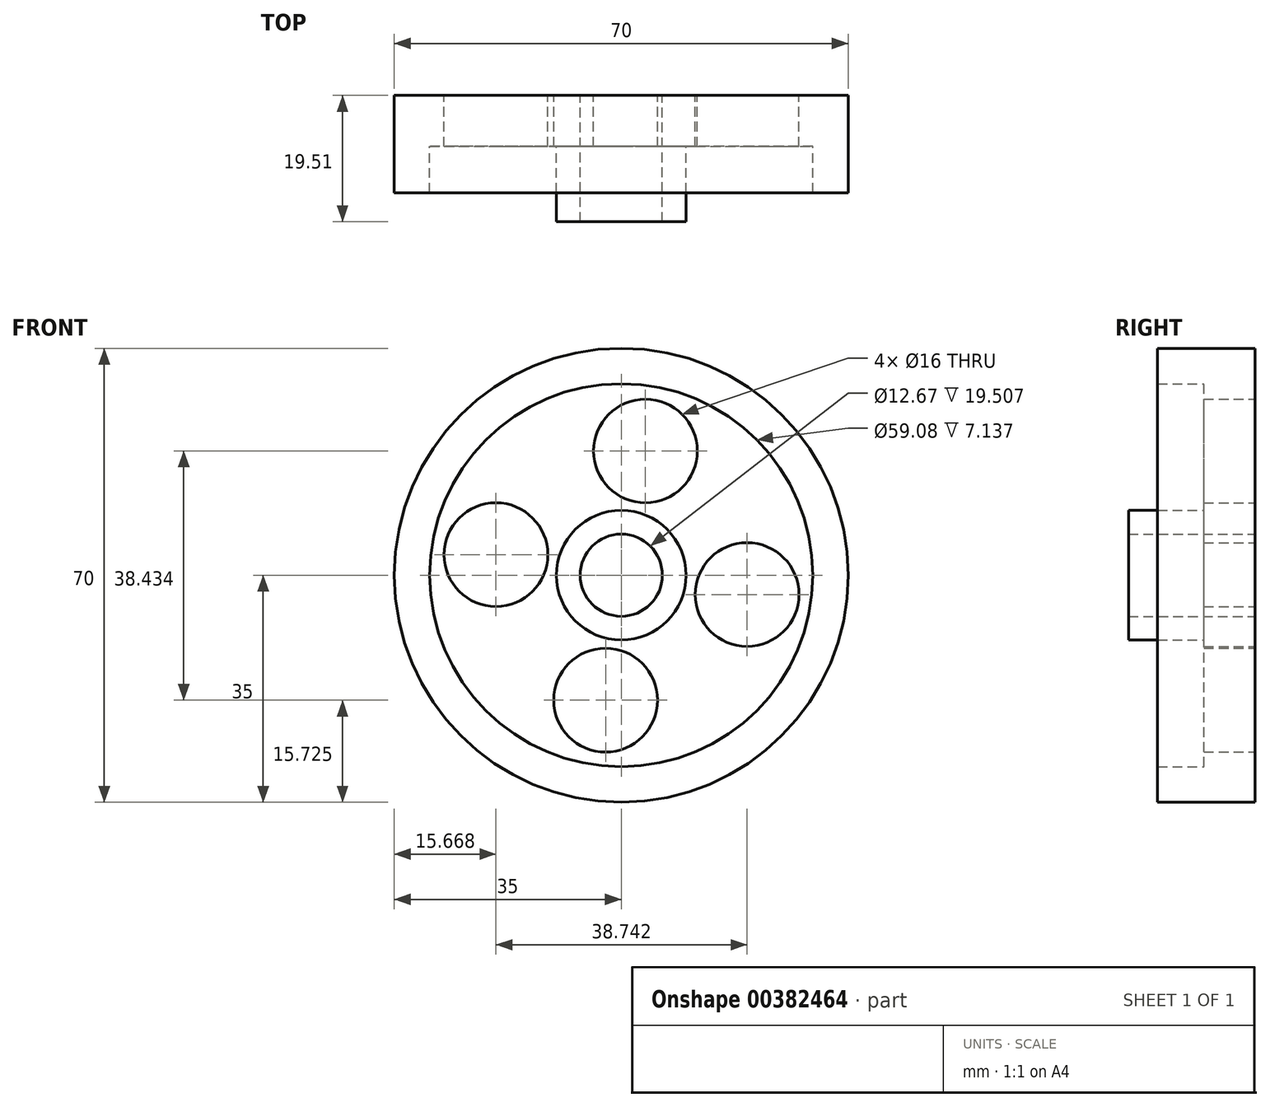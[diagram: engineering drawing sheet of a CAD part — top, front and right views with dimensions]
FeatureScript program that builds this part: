
annotation { "Feature Type Name" : "Feature", "Feature Type Description" : "" }
export const myFeature = defineFeature(function(context is Context, id is Id, definition is map)
    precondition{}
    {
        {
            var Q0;
            Q0=qCreatedBy(makeId("Front.planeOp"),FACE);
            var sketch = newSketch(context, id + "F0", { "sketchPlane" : qUnion([Q0])});
            skCircle(sketch, "E0", {"center": v(0, 0) * mm, "radius": 35 * mm});
            skCircle(sketch, "E1", {"center": v(0, 0) * mm, "radius": 29.54 * mm});
            skCircle(sketch, "E2", {"center": v(0, 0) * mm, "radius": 10 * mm});
            skCircle(sketch, "E3", {"center": v(0, 0) * mm, "radius": 6.34 * mm});
            skCircle(sketch, "E4", {"center": v(3.73, 19.16) * mm, "radius": 8 * mm});
            skCircle(sketch, "E5", {"center": v(-19.33, 3.17) * mm, "radius": 8 * mm});
            skCircle(sketch, "E6", {"center": v(-2.42, -19.28) * mm, "radius": 8 * mm});
            skCircle(sketch, "E7", {"center": v(19.4, -2.98) * mm, "radius": 8 * mm});
            skSolve(sketch);
        }
        {
            var Q0;
            Q0=makeQuery(id+"F0.imprint","IMPRINT",FACE,{"disambiguationData":[TD([[makeQuery(id+"F0.imprint","IMPRINT",EDGE,{"derivedFrom":sQuery(id+"F0.wireOp",EDGE,"E2")}),1.0]])]});
            extrude(context, id + "F1", {"entities" : qUnion([Q0]), "depth" : 19.5 * mm});
        }
        {
            var Q0;
            Q0=makeQuery(id+"F0.imprint","IMPRINT",FACE,{"disambiguationData":[TD([[makeQuery(id+"F0.imprint","IMPRINT",EDGE,{"derivedFrom":sQuery(id+"F0.wireOp",EDGE,"E1")}),1.0]])]});
            extrude(context, id + "F2", {"entities" : qUnion([Q0]), "operationType" : NewBodyOperationType.ADD, "depth" : 7.87 * mm});
        }
        {
            var Q0;
            Q0=makeQuery(id+"F0.imprint","IMPRINT",FACE,{"disambiguationData":[TD([[makeQuery(id+"F0.imprint","IMPRINT",EDGE,{"derivedFrom":sQuery(id+"F0.wireOp",EDGE,"E0")}),1.0]])]});
            extrude(context, id + "F3", {"entities" : qUnion([Q0]), "operationType" : NewBodyOperationType.ADD, "depth" : 15 * mm});
        }
    });
